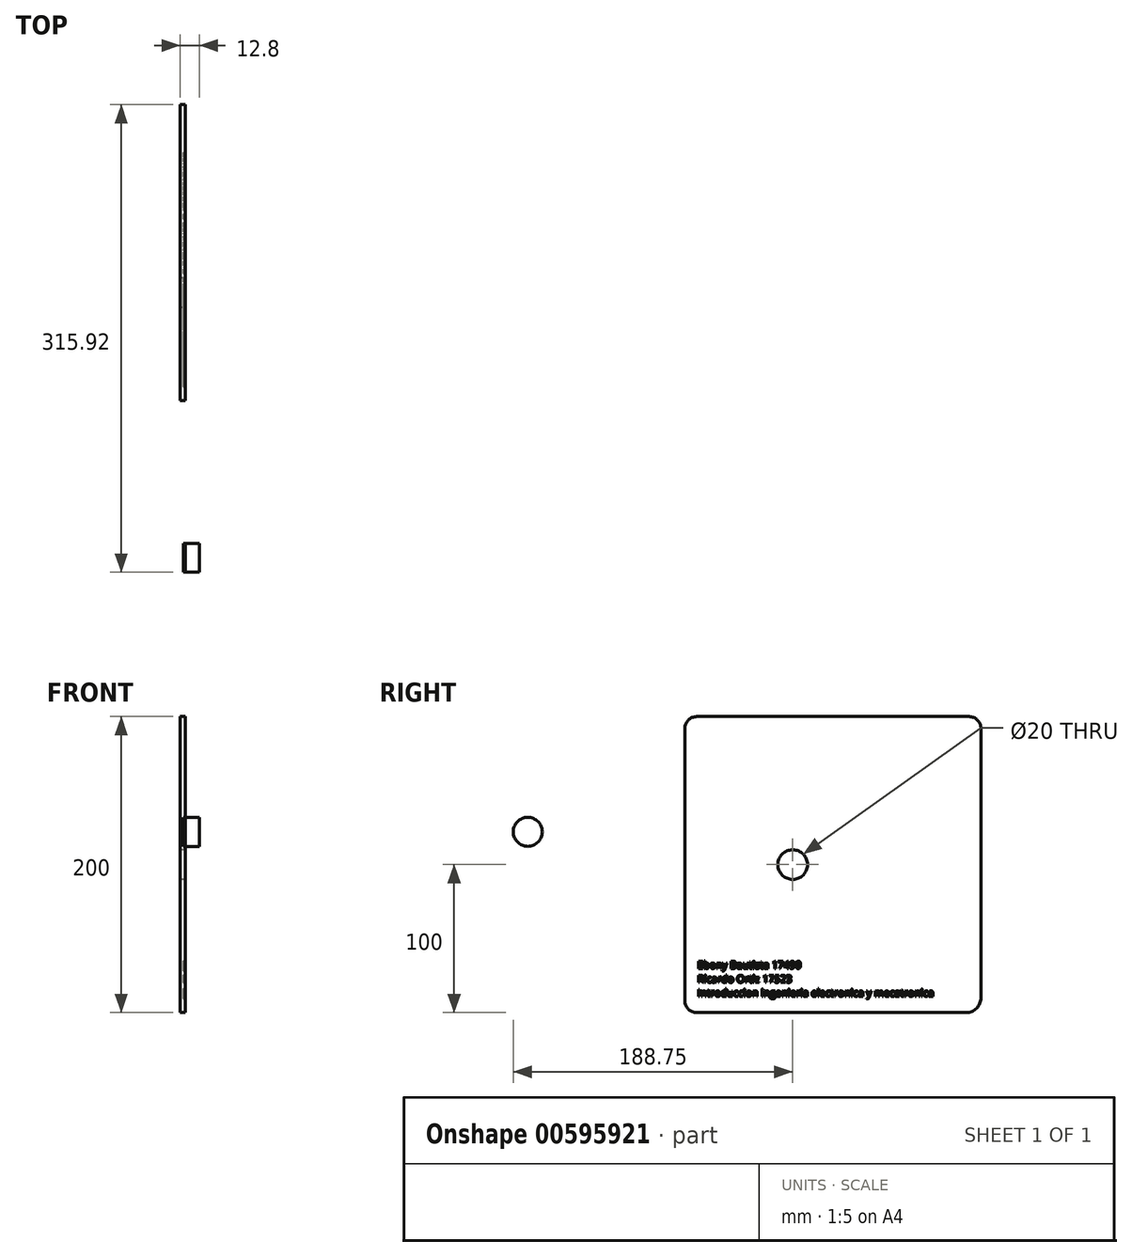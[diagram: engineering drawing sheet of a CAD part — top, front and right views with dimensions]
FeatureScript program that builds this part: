
annotation { "Feature Type Name" : "Feature", "Feature Type Description" : "" }
export const myFeature = defineFeature(function(context is Context, id is Id, definition is map)
    precondition{}
    {
        {
            var Q0;
            Q0=qCreatedBy(makeId("Right.planeOp"),FACE);
            var sketch = newSketch(context, id + "F0", { "sketchPlane" : qUnion([Q0])});
            skLineSegment(sketch, "E0.bottom", {"start": v(-118, 100) * mm, "end": v(82, 100) * mm});
            skLineSegment(sketch, "E0.top", {"start": v(-118, -100) * mm, "end": v(82, -100) * mm});
            skLineSegment(sketch, "E0.left", {"start": v(-118, 100) * mm, "end": v(-118, -100) * mm});
            skLineSegment(sketch, "E0.right", {"start": v(82, 100) * mm, "end": v(82, -100) * mm});
            skCircle(sketch, "E1", {"center": v(-45.17, 0) * mm, "radius": 10 * mm});
            skSolve(sketch);
        }
        {
            var Q0;
            Q0=qSketchRegion(id+"F0",true);
            extrude(context, id + "F1", {"entities" : qUnion([Q0]), "depth" : 3.2 * mm, "offsetDistance" : 25 * mm});
        }
        {
            var Q0;
            Q0=makeQuery(id+"F1.opExtrude","SWEPT_EDGE",EDGE,{"disambiguationData":[OSD([sQuery(id+"F0.wireOp",EDGE,"E0.bottom"),sQuery(id+"F0.wireOp",EDGE,"E0.left")])]});
            var Q1;
            Q1=makeQuery(id+"F1.opExtrude","SWEPT_EDGE",EDGE,{"disambiguationData":[OSD([sQuery(id+"F0.wireOp",EDGE,"E0.top"),sQuery(id+"F0.wireOp",EDGE,"E0.left")])]});
            var Q2;
            Q2=makeQuery(id+"F1.opExtrude","SWEPT_EDGE",EDGE,{"disambiguationData":[OSD([sQuery(id+"F0.wireOp",EDGE,"E0.bottom"),sQuery(id+"F0.wireOp",EDGE,"E0.right")])]});
            fillet(context, id + "F2", {"entities" : qUnion([Q0, Q1, Q2]), "radius" : 8 * mm, "tangentPropagation" : true, "allowEdgeOverflow" : false});
        }
        {
            var Q0;
            Q0=makeQuery(id+"F1.opExtrude","CAP_FACE",FACE,{"disambiguationData":[OSD([sQuery(id+"F0.wireOp",EDGE,"E0.bottom"),sQuery(id+"F0.wireOp",EDGE,"E0.top"),sQuery(id+"F0.wireOp",EDGE,"E0.left"),sQuery(id+"F0.wireOp",EDGE,"E0.right"),sQuery(id+"F0.wireOp",EDGE,"E1")])],"isStart":false});
            var sketch = newSketch(context, id + "F3", { "sketchPlane" : qUnion([Q0])});
            skCircle(sketch, "E2", {"center": v(-224.12, 22.14) * mm, "radius": 9.8 * mm});
            skText(sketch, "E3", { "text": "Ebony Bautista 17490\nRicardo Ortiz 17523\nIntroduccion ingenieria electronica y mecatronica", "fontName": "OpenSans-Regular.ttf"});
            const initialGuessF3  = {"E3": [-0.1094, -0.07023, 1, 0, 0.005]};
            skSetInitialGuess(sketch, initialGuessF3);
            skSolve(sketch);
        }
        {
            var Q0;
            Q0=makeQuery(id+"F3.imprint","IMPRINT",FACE,{"disambiguationData":[TD([[makeQuery(id+"F3.imprint","IMPRINT",EDGE,{"derivedFrom":sQuery(id+"F3.wireOp",EDGE,"E2")}),1.0]])]});
            extrude(context, id + "F4", {"entities" : qUnion([Q0]), "depth" : 9.6 * mm, "offsetDistance" : 25 * mm});
        }
        {
            var Q0;
            Q0=makeQuery(id+"F1.opExtrude","SWEPT_EDGE",EDGE,{"disambiguationData":[OSD([sQuery(id+"F0.wireOp",EDGE,"E0.top"),sQuery(id+"F0.wireOp",EDGE,"E0.right")])]});
            fillet(context, id + "F5", {"entities" : qUnion([Q0]), "radius" : 10 * mm, "tangentPropagation" : true, "allowEdgeOverflow" : false});
        }
        {
            var Q0;
            Q0=qSketchRegion(id+"F3",true);
            extrude(context, id + "F6", {"entities" : qUnion([Q0]), "oppositeDirection" : true, "depth" : 1 * mm, "offsetDistance" : 25 * mm});
        }
    });
